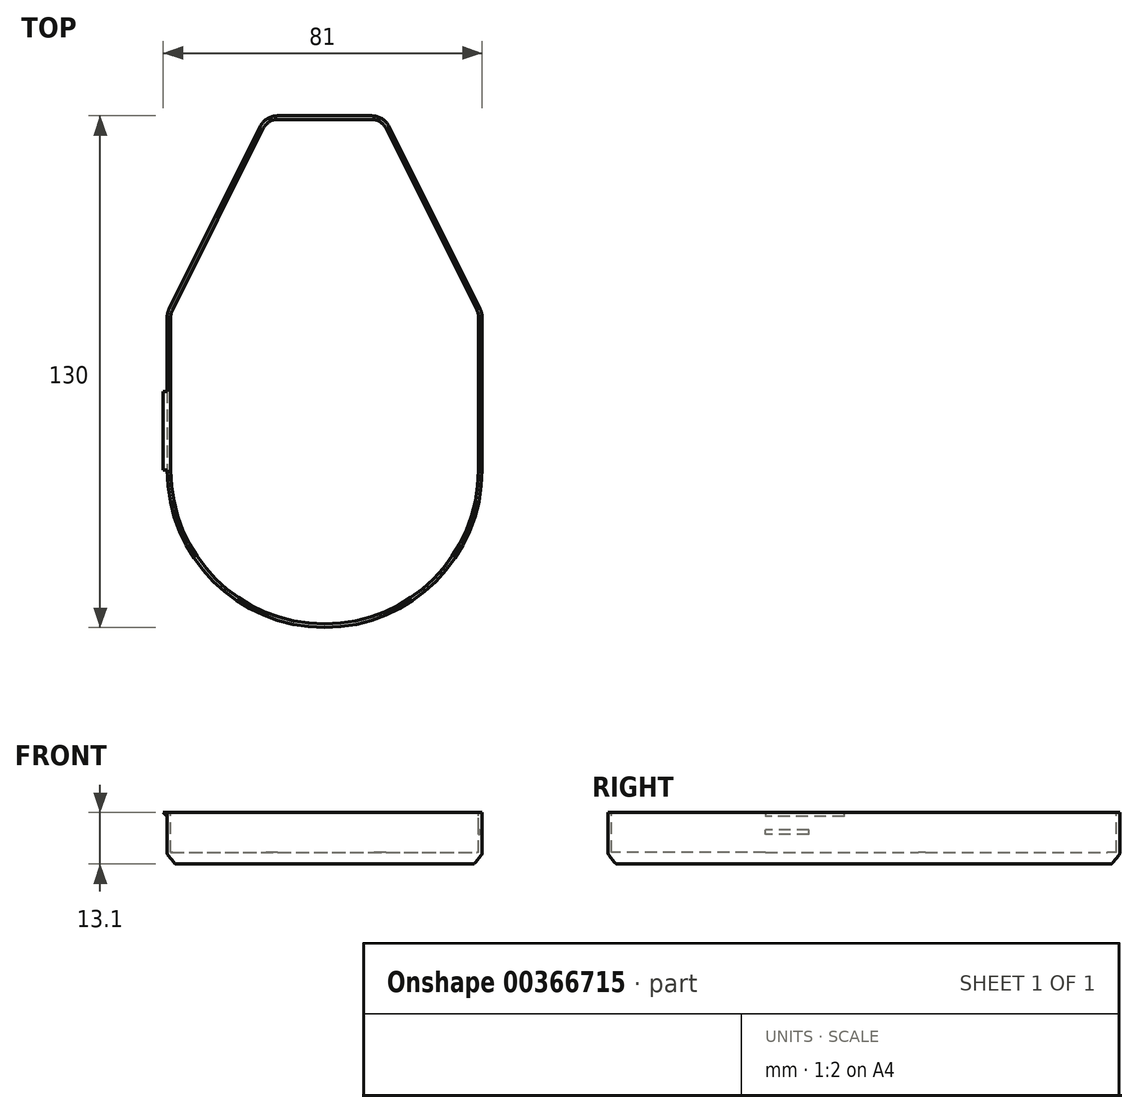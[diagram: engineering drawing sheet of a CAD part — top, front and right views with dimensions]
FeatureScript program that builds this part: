
annotation { "Feature Type Name" : "Feature", "Feature Type Description" : "" }
export const myFeature = defineFeature(function(context is Context, id is Id, definition is map)
    precondition{}
    {
        {
            var Q0;
            Q0=qCreatedBy(makeId("Top.planeOp"),FACE);
            var sketch = newSketch(context, id + "F0", { "sketchPlane" : qUnion([Q0])});
            skArc(sketch, "E0", {"start": v(-40, 0) * mm, "mid": v(0, -40) * mm, "end": v(40, 0) * mm});
            skLineSegment(sketch, "E1", {"start": v(-40, 0) * mm, "end": v(-40, 38.82) * mm});
            skLineSegment(sketch, "E2", {"start": v(-39.47, 41.06) * mm, "end": v(-16.38, 87.24) * mm});
            skLineSegment(sketch, "E3", {"start": v(-11.9, 90) * mm, "end": v(11.9, 90) * mm});
            skLineSegment(sketch, "E4", {"start": v(16.38, 87.24) * mm, "end": v(39.47, 41.06) * mm});
            skLineSegment(sketch, "E5", {"start": v(40, 38.82) * mm, "end": v(40, 0) * mm});
            skPoint(sketch, "E6.visualSharp", {"position": v(-15, 90) * mm});
            skArc(sketch, "E6.filletArc", {"start": v(-11.9, 90) * mm, "mid": v(-14.54, 89.25) * mm, "end": v(-16.38, 87.24) * mm});
            skPoint(sketch, "E7.visualSharp", {"position": v(15, 90) * mm});
            skArc(sketch, "E7.filletArc", {"start": v(16.38, 87.24) * mm, "mid": v(14.54, 89.25) * mm, "end": v(11.9, 90) * mm});
            skPoint(sketch, "E8.visualSharp", {"position": v(-40, 40) * mm});
            skArc(sketch, "E8.filletArc", {"start": v(-39.47, 41.06) * mm, "mid": v(-39.87, 39.97) * mm, "end": v(-40, 38.82) * mm});
            skPoint(sketch, "E9.visualSharp", {"position": v(40, 40) * mm});
            skArc(sketch, "E9.filletArc", {"start": v(40, 38.82) * mm, "mid": v(39.87, 39.97) * mm, "end": v(39.47, 41.06) * mm});
            skSolve(sketch);
        }
        {
            var Q0;
            Q0 = qSketchRegion(id + "F0", true);
            extrude(context, id + "F1", {"entities" : qUnion([Q0]), "depth" : 13.1 * mm});
        }
        {
            var Q0;
            Q0=makeQuery(id+"F1.opExtrude","CAP_FACE",FACE,{"disambiguationData":[OSD([sQuery(id+"F0.wireOp",EDGE,"E0"),sQuery(id+"F0.wireOp",EDGE,"E1"),sQuery(id+"F0.wireOp",EDGE,"E2"),sQuery(id+"F0.wireOp",EDGE,"E3"),sQuery(id+"F0.wireOp",EDGE,"E4"),sQuery(id+"F0.wireOp",EDGE,"E5"),sQuery(id+"F0.wireOp",EDGE,"E6.filletArc"),sQuery(id+"F0.wireOp",EDGE,"E7.filletArc"),sQuery(id+"F0.wireOp",EDGE,"E8.filletArc"),sQuery(id+"F0.wireOp",EDGE,"E9.filletArc")])],"isStart":false});
            var sketch = newSketch(context, id + "F2", { "sketchPlane" : qUnion([Q0])});
            skArc(sketch, "E10.0", {"start": v(-11.9, 89.1) * mm, "mid": v(-14.07, 88.49) * mm, "end": v(-15.58, 86.83) * mm});
            skLineSegment(sketch, "E10.1", {"start": v(-38.67, 40.65) * mm, "end": v(-15.58, 86.83) * mm});
            skLineSegment(sketch, "E10.2", {"start": v(-11.9, 89.1) * mm, "end": v(11.9, 89.1) * mm});
            skArc(sketch, "E10.3", {"start": v(-38.67, 40.65) * mm, "mid": v(-39, 39.76) * mm, "end": v(-39.1, 38.82) * mm});
            skLineSegment(sketch, "E10.4", {"start": v(-39.1, 0) * mm, "end": v(-39.1, 38.82) * mm});
            skArc(sketch, "E10.5", {"start": v(-39.1, 0) * mm, "mid": v(0, -39.1) * mm, "end": v(39.1, 0) * mm});
            skArc(sketch, "E10.6", {"start": v(15.58, 86.83) * mm, "mid": v(14.07, 88.49) * mm, "end": v(11.9, 89.1) * mm});
            skLineSegment(sketch, "E10.7", {"start": v(15.58, 86.83) * mm, "end": v(38.67, 40.65) * mm});
            skArc(sketch, "E10.8", {"start": v(39.1, 38.82) * mm, "mid": v(39, 39.76) * mm, "end": v(38.67, 40.65) * mm});
            skLineSegment(sketch, "E10.9", {"start": v(39.1, 38.82) * mm, "end": v(39.1, 0) * mm});
            skSolve(sketch);
        }
        {
            var Q0;
            Q0 = qSketchRegion(id + "F2", true);
            extrude(context, id + "F3", {"entities" : qUnion([Q0]), "operationType" : NewBodyOperationType.REMOVE, "oppositeDirection" : true, "depth" : 10.1 * mm});
        }
        {
            var Q0;
            Q0=qCreatedBy(makeId("Front.planeOp"),FACE);
            var sketch = newSketch(context, id + "F4", { "sketchPlane" : qUnion([Q0])});
            skCircle(sketch, "E11", {"center": v(39.05, 8.1) * mm, "radius": 0.6 * mm});
            skSolve(sketch);
        }
        {
            var Q0;
            Q0 = qSketchRegion(id + "F4", true);
            extrude(context, id + "F5", {"entities" : qUnion([Q0]), "operationType" : NewBodyOperationType.REMOVE, "oppositeDirection" : true, "depth" : 11 * mm});
        }
        {
            var Q0;
            Q0=qCreatedBy(makeId("Front.planeOp"),FACE);
            var sketch = newSketch(context, id + "F6", { "sketchPlane" : qUnion([Q0])});
            skLineSegment(sketch, "E12", {"start": v(-40, 12.1) * mm, "end": v(-40, 13.1) * mm});
            skLineSegment(sketch, "E13", {"start": v(-40, 13.1) * mm, "end": v(-41, 13.1) * mm});
            skLineSegment(sketch, "E14", {"start": v(-41, 13.1) * mm, "end": v(-40, 12.1) * mm});
            skSolve(sketch);
        }
        {
            var Q0;
            Q0 = qSketchRegion(id + "F6", true);
            extrude(context, id + "F7", {"entities" : qUnion([Q0]), "operationType" : NewBodyOperationType.ADD, "oppositeDirection" : true, "depth" : 20 * mm});
        }
        {
            var Q0;
            Q0=makeQuery(id+"F1.opExtrude","CAP_FACE",FACE,{"disambiguationData":[OSD([sQuery(id+"F0.wireOp",EDGE,"E0"),sQuery(id+"F0.wireOp",EDGE,"E1"),sQuery(id+"F0.wireOp",EDGE,"E2"),sQuery(id+"F0.wireOp",EDGE,"E3"),sQuery(id+"F0.wireOp",EDGE,"E4"),sQuery(id+"F0.wireOp",EDGE,"E5"),sQuery(id+"F0.wireOp",EDGE,"E6.filletArc"),sQuery(id+"F0.wireOp",EDGE,"E7.filletArc"),sQuery(id+"F0.wireOp",EDGE,"E8.filletArc"),sQuery(id+"F0.wireOp",EDGE,"E9.filletArc")])],"isStart":true});
            chamfer(context, id + "F8", {"entities" : qUnion([Q0]), "chamferType" : ChamferType.TWO_OFFSETS, "width1" : 2.5 * mm, "oppositeDirection" : false, "width2" : 2 * mm, "tangentPropagation" : true});
        }
        {
            var Q0;
            Q0=makeQuery(id+"F1.opExtrude","CAP_FACE",FACE,{"disambiguationData":[OSD([sQuery(id+"F0.wireOp",EDGE,"E0"),sQuery(id+"F0.wireOp",EDGE,"E1"),sQuery(id+"F0.wireOp",EDGE,"E2"),sQuery(id+"F0.wireOp",EDGE,"E3"),sQuery(id+"F0.wireOp",EDGE,"E4"),sQuery(id+"F0.wireOp",EDGE,"E5"),sQuery(id+"F0.wireOp",EDGE,"E6.filletArc"),sQuery(id+"F0.wireOp",EDGE,"E7.filletArc"),sQuery(id+"F0.wireOp",EDGE,"E8.filletArc"),sQuery(id+"F0.wireOp",EDGE,"E9.filletArc")])],"isStart":true});
            var Q1;
            {var subQ0=sQuery(id+"F0.wireOp",EDGE,"E0");Q1=makeQuery(id+"F8.opChamfer","BLEND_EDGE",EDGE,{"blendedFrom":[makeQuery(id+"F1.opExtrude","CAP_EDGE",EDGE,{"disambiguationData":[OSD([subQ0])],"isStart":true}),makeQuery(id+"F1.opExtrude","SWEPT_FACE",FACE,{"disambiguationData":[OSD([subQ0])]})],"blendedInto":[makeQuery(id+"F1.opExtrude","SWEPT_FACE",FACE,{"disambiguationData":[OSD([subQ0])]})]});}
            fillet(context, id + "F9", {"entities" : qUnion([Q0, Q1]), "radius" : 1 * mm, "tangentPropagation" : true, "allowEdgeOverflow" : false});
        }
    });
